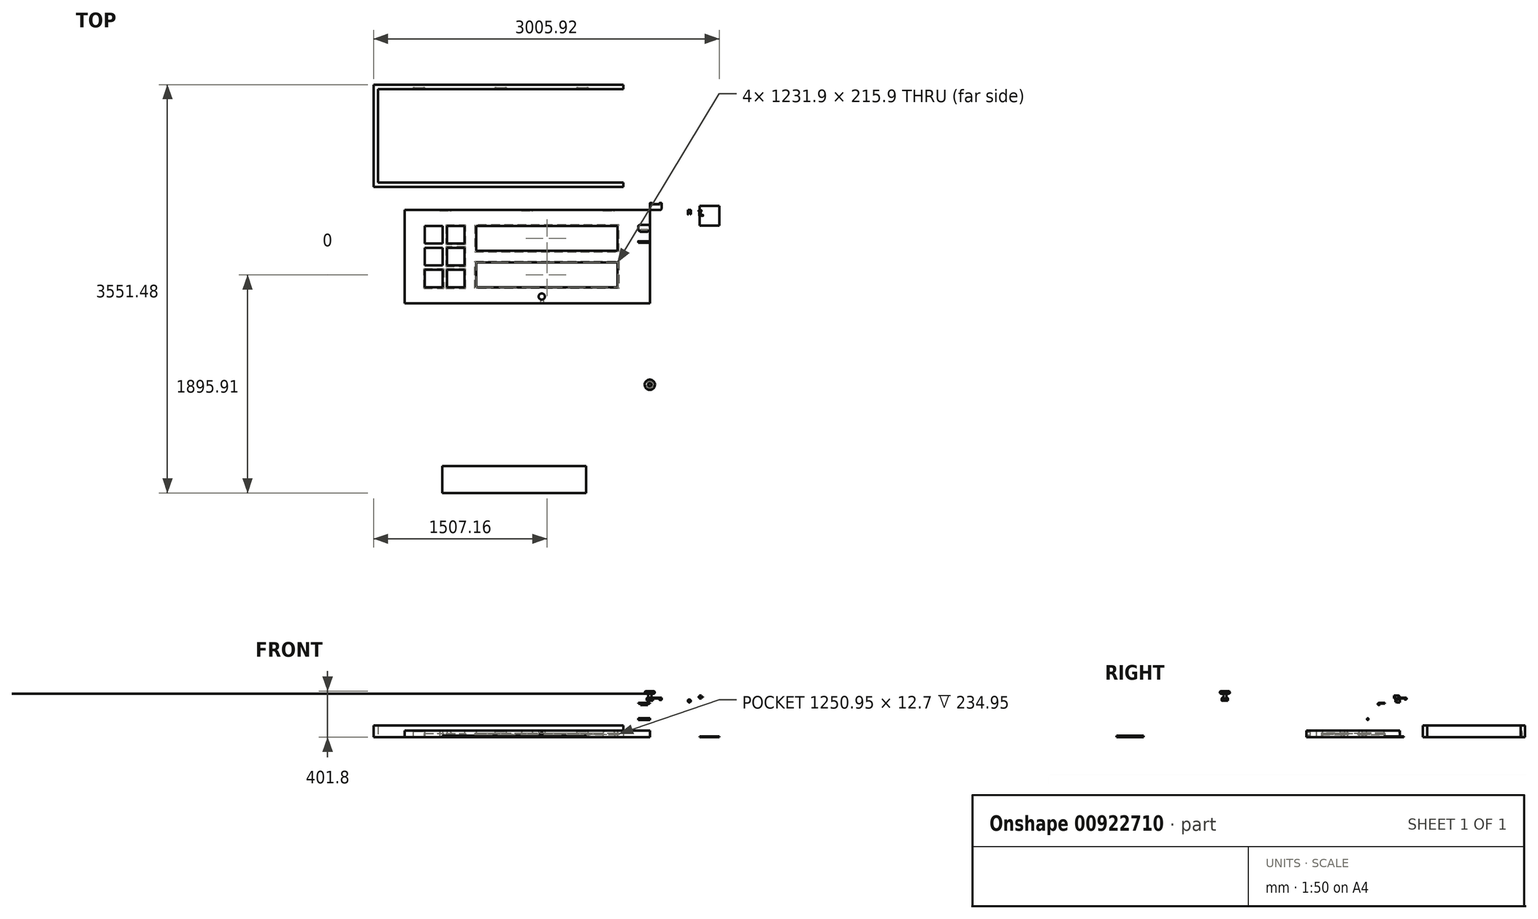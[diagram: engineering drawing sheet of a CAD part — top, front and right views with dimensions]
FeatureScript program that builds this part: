
annotation { "Feature Type Name" : "Feature", "Feature Type Description" : "" }
export const myFeature = defineFeature(function(context is Context, id is Id, definition is map)
    precondition{}
    {
        {
            var Q0;
            Q0=qCreatedBy(makeId("Top.planeOp"),FACE);
            var sketch = newSketch(context, id + "F0", { "sketchPlane" : qUnion([Q0])});
            skLineSegment(sketch, "E0", {"start": v(0, 0) * mm, "end": v(0, -812.8) * mm});
            skLineSegment(sketch, "E1", {"start": v(0, -812.8) * mm, "end": v(-2133.6, -812.8) * mm});
            skLineSegment(sketch, "E2", {"start": v(-2133.6, -812.8) * mm, "end": v(-2133.6, 0) * mm});
            skLineSegment(sketch, "E3", {"start": v(-2133.6, 0) * mm, "end": v(0, 0) * mm});
            skLineSegment(sketch, "E4.bottom", {"start": v(-1955.8, -673.1) * mm, "end": v(-1803.4, -673.1) * mm});
            skLineSegment(sketch, "E4.top", {"start": v(-1955.8, -139.7) * mm, "end": v(-1803.4, -139.7) * mm});
            skLineSegment(sketch, "E4.left", {"start": v(-1955.8, -673.1) * mm, "end": v(-1955.8, -520.7) * mm});
            skLineSegment(sketch, "E4.right", {"start": v(-1612.9, -673.1) * mm, "end": v(-1612.9, -520.7) * mm});
            skLineSegment(sketch, "E5", {"start": v(-1612.9, -482.6) * mm, "end": v(-1612.9, -330.2) * mm});
            skLineSegment(sketch, "E6.0.left", {"start": v(-1955.8, -482.6) * mm, "end": v(-1803.4, -482.6) * mm});
            skLineSegment(sketch, "E6.0.right", {"start": v(-1955.8, -520.7) * mm, "end": v(-1803.4, -520.7) * mm});
            skLineSegment(sketch, "E6.1.left", {"start": v(-1765.3, -139.7) * mm, "end": v(-1765.3, -292.1) * mm});
            skLineSegment(sketch, "E6.1.right", {"start": v(-1803.4, -139.7) * mm, "end": v(-1803.4, -292.1) * mm});
            skLineSegment(sketch, "E6.2.left", {"start": v(-1612.9, -330.2) * mm, "end": v(-1765.3, -330.2) * mm});
            skLineSegment(sketch, "E6.2.right", {"start": v(-1612.9, -292.1) * mm, "end": v(-1765.3, -292.1) * mm});
            skPoint(sketch, "E7.orphan", {"position": v(-1955.8, -351.36) * mm});
            skPoint(sketch, "E8.orphan", {"position": v(-1955.8, -461.44) * mm});
            skLineSegment(sketch, "E9.trimOffspring", {"start": v(-1803.4, -520.7) * mm, "end": v(-1803.4, -673.1) * mm});
            skLineSegment(sketch, "E10.trimOffspring", {"start": v(-1765.3, -520.7) * mm, "end": v(-1612.9, -520.7) * mm});
            skLineSegment(sketch, "E11.trimOffspring", {"start": v(-1765.3, -520.7) * mm, "end": v(-1765.3, -673.1) * mm});
            skLineSegment(sketch, "E12.trimOffspring", {"start": v(-1765.3, -482.6) * mm, "end": v(-1612.9, -482.6) * mm});
            skLineSegment(sketch, "E13.trimOffspring", {"start": v(-1803.4, -292.1) * mm, "end": v(-1955.8, -292.1) * mm});
            skLineSegment(sketch, "E14.trimOffspring", {"start": v(-1803.4, -330.2) * mm, "end": v(-1803.4, -482.6) * mm});
            skLineSegment(sketch, "E15.trimOffspring", {"start": v(-1803.4, -330.2) * mm, "end": v(-1955.8, -330.2) * mm});
            skLineSegment(sketch, "E16.trimOffspring", {"start": v(-1765.3, -330.2) * mm, "end": v(-1765.3, -482.6) * mm});
            skPoint(sketch, "E6.1.startCap.center.orphan", {"position": v(-1784.35, -139.7) * mm});
            skPoint(sketch, "E6.1.endCap.center.orphan", {"position": v(-1784.35, -673.1) * mm});
            skLineSegment(sketch, "E17.trimOffspring", {"start": v(-1955.8, -482.6) * mm, "end": v(-1955.8, -330.2) * mm});
            skLineSegment(sketch, "E18.trimOffspring", {"start": v(-1955.8, -292.1) * mm, "end": v(-1955.8, -139.7) * mm});
            skLineSegment(sketch, "E19.trimOffspring", {"start": v(-1612.9, -292.1) * mm, "end": v(-1612.9, -139.7) * mm});
            skLineSegment(sketch, "E20.trimOffspring", {"start": v(-1765.3, -673.1) * mm, "end": v(-1612.9, -673.1) * mm});
            skLineSegment(sketch, "E21.trimOffspring", {"start": v(-1765.3, -139.7) * mm, "end": v(-1612.9, -139.7) * mm});
            skLineSegment(sketch, "E22.bottom", {"start": v(-1511.3, -673.1) * mm, "end": v(-279.4, -673.1) * mm});
            skLineSegment(sketch, "E22.top", {"start": v(-1511.3, -139.7) * mm, "end": v(-279.4, -139.7) * mm});
            skLineSegment(sketch, "E22.left", {"start": v(-1511.3, -673.1) * mm, "end": v(-1511.3, -457.2) * mm});
            skLineSegment(sketch, "E22.right", {"start": v(-279.4, -673.1) * mm, "end": v(-279.4, -457.2) * mm});
            skLineSegment(sketch, "E23.0.left", {"start": v(-1511.3, -355.6) * mm, "end": v(-279.4, -355.6) * mm});
            skLineSegment(sketch, "E23.0.right", {"start": v(-1511.3, -457.2) * mm, "end": v(-279.4, -457.2) * mm});
            skPoint(sketch, "E24.start.orphan", {"position": v(-1511.3, -406.4) * mm});
            skLineSegment(sketch, "E25.trimOffspring", {"start": v(-1511.3, -355.6) * mm, "end": v(-1511.3, -139.7) * mm});
            skLineSegment(sketch, "E26.trimOffspring", {"start": v(-279.4, -355.6) * mm, "end": v(-279.4, -139.7) * mm});
            skPoint(sketch, "E23.0.endCap.center.orphan", {"position": v(-279.4, -406.4) * mm});
            skSolve(sketch);
        }
        {
            var Q0;
            Q0=makeQuery(id+"F0.imprint","IMPRINT",FACE,{"disambiguationData":[TD([[makeQuery(id+"F0.imprint","IMPRINT",EDGE,{"derivedFrom":sQuery(id+"F0.wireOp",EDGE,"E0")}),-1.0]])]});
            extrude(context, id + "F1", {"entities" : qUnion([Q0]), "depth" : 57.15 * mm, "offsetDistance" : 25.4 * mm});
        }
        {
            var Q0;
            Q0=qCreatedBy(makeId("Right.planeOp"),FACE);
            var sketch = newSketch(context, id + "F2", { "sketchPlane" : qUnion([Q0])});
            skLineSegment(sketch, "E27", {"start": v(41.82, 339.3) * mm, "end": v(0, 339.3) * mm});
            skLineSegment(sketch, "E28", {"start": v(0, 339.3) * mm, "end": v(0, 345.66) * mm});
            skLineSegment(sketch, "E29", {"start": v(0, 345.66) * mm, "end": v(50.8, 345.66) * mm});
            skArc(sketch, "E30", {"start": v(41.82, 339.3) * mm, "mid": v(56.3, 328.36) * mm, "end": v(50.8, 345.66) * mm});
            skCircle(sketch, "E31.0", {"center": v(50.8, 336.13) * mm, "radius": 6.99 * mm});
            skPoint(sketch, "E32.end.orphan", {"position": v(50.8, 339.3) * mm});
            skSolve(sketch);
        }
        {
            var Q0;
            Q0=makeQuery(id+"F2.imprint","IMPRINT",FACE,{"disambiguationData":[TD([[makeQuery(id+"F2.imprint","IMPRINT",EDGE,{"derivedFrom":sQuery(id+"F2.wireOp",EDGE,"E27")}),-1.0]])]});
            extrude(context, id + "F3", {"entities" : qUnion([Q0]), "depth" : 101.6 * mm, "offsetDistance" : 25.4 * mm});
        }
        {
            var Q0;
            Q0=makeQuery(id+"F3.opExtrude","CAP_FACE",FACE,{"disambiguationData":[OSD([sQuery(id+"F2.wireOp",EDGE,"E27"),sQuery(id+"F2.wireOp",EDGE,"E28"),sQuery(id+"F2.wireOp",EDGE,"E29"),sQuery(id+"F2.wireOp",EDGE,"E30"),sQuery(id+"F2.wireOp",EDGE,"E31.0")])],"isStart":false});
            cPlane(context, id + "F4", {"entities" : qUnion([Q0]), "cplaneType" : CPlaneType.OFFSET, "offset" : 19.05 * mm, "oppositeDirection" : true, "width" : 152.4 * mm, "height" : 152.4 * mm});
        }
        {
            var Q0;
            Q0=qCreatedBy(id+"F4.planeOp",FACE);
            var sketch = newSketch(context, id + "F5", { "sketchPlane" : qUnion([Q0])});
            skCircle(sketch, "E33", {"center": v(50.8, 336.13) * mm, "radius": 9.53 * mm});
            skLineSegment(sketch, "E34", {"start": v(50.8, 336.13) * mm, "end": v(50.8, 345.66) * mm});
            skSolve(sketch);
        }
        {
            var Q0;
            Q0 = qSketchRegion(id + "F5", true);
            extrude(context, id + "F6", {"entities" : qUnion([Q0]), "operationType" : NewBodyOperationType.REMOVE, "oppositeDirection" : true, "depth" : 63.5 * mm, "offsetDistance" : 25.4 * mm});
        }
        {
            var Q0;
            Q0=qCreatedBy(makeId("Right.planeOp"),FACE);
            var sketch = newSketch(context, id + "F7", { "sketchPlane" : qUnion([Q0])});
            skLineSegment(sketch, "E35", {"start": v(-172.18, 292.28) * mm, "end": v(-130.36, 292.28) * mm});
            skLineSegment(sketch, "E36", {"start": v(-130.36, 292.28) * mm, "end": v(-130.36, 298.63) * mm});
            skLineSegment(sketch, "E37", {"start": v(-130.36, 298.63) * mm, "end": v(-181.16, 298.63) * mm});
            skArc(sketch, "E38", {"start": v(-172.18, 292.28) * mm, "mid": v(-175.66, 296.88) * mm, "end": v(-181.16, 298.63) * mm});
            skPoint(sketch, "E39", {"position": v(-181.16, 298.63) * mm});
            skPoint(sketch, "E40.orphan", {"position": v(-181.16, 292.28) * mm});
            skSolve(sketch);
        }
        {
            var Q0;
            Q0 = qSketchRegion(id + "F7", true);
            extrude(context, id + "F8", {"entities" : qUnion([Q0]), "oppositeDirection" : true, "depth" : 101.6 * mm, "offsetDistance" : 25.4 * mm});
        }
        {
            var Q0;
            Q0=makeQuery(id+"F8.opExtrude","CAP_FACE",FACE,{"disambiguationData":[OSD([sQuery(id+"F7.wireOp",EDGE,"E35"),sQuery(id+"F7.wireOp",EDGE,"E36"),sQuery(id+"F7.wireOp",EDGE,"E37"),sQuery(id+"F7.wireOp",EDGE,"E38")])],"isStart":true});
            cPlane(context, id + "F9", {"entities" : qUnion([Q0]), "cplaneType" : CPlaneType.OFFSET, "offset" : 50.8 * mm, "oppositeDirection" : true, "width" : 152.4 * mm, "height" : 152.4 * mm});
        }
        {
            var Q0;
            Q0=qCreatedBy(id+"F9.planeOp",FACE);
            var sketch = newSketch(context, id + "F10", { "sketchPlane" : qUnion([Q0])});
            skCircle(sketch, "E41", {"center": v(-181.16, 289.1) * mm, "radius": 9.53 * mm});
            skPoint(sketch, "E42", {"position": v(-181.16, 298.63) * mm});
            skCircle(sketch, "E43.0", {"center": v(-181.16, 289.1) * mm, "radius": 6.99 * mm});
            skSolve(sketch);
        }
        {
            var Q0;
            Q0=makeQuery(id+"F10.imprint","IMPRINT",FACE,{"disambiguationData":[TD([[makeQuery(id+"F10.imprint","IMPRINT",EDGE,{"derivedFrom":sQuery(id+"F10.wireOp",EDGE,"E41")}),1.0]])]});
            extrude(context, id + "F11", {"entities" : qUnion([Q0]), "operationType" : NewBodyOperationType.ADD, "endBound" : BoundingType.SYMMETRIC, "depth" : 63.5 * mm, "offsetDistance" : 25.4 * mm});
        }
        {
            var Q0;
            Q0=qCreatedBy(makeId("Right.planeOp"),FACE);
            var sketch = newSketch(context, id + "F12", { "sketchPlane" : qUnion([Q0])});
            skCircle(sketch, "E44", {"center": v(-277.25, 157.74) * mm, "radius": 6.99 * mm});
            skSolve(sketch);
        }
        {
            var Q0;
            Q0 = qSketchRegion(id + "F12", true);
            extrude(context, id + "F13", {"entities" : qUnion([Q0]), "oppositeDirection" : true, "depth" : 101.6 * mm, "offsetDistance" : 25.4 * mm});
        }
        {
            var Q0;
            Q0=makeQuery(id+"F8.opExtrude","CAP_EDGE",EDGE,{"disambiguationData":[OSD([sQuery(id+"F7.wireOp",EDGE,"E36")])],"isStart":true});
            var Q1;
            Q1=makeQuery(id+"F8.opExtrude","CAP_EDGE",EDGE,{"disambiguationData":[OSD([sQuery(id+"F7.wireOp",EDGE,"E36")])],"isStart":false});
            var Q2;
            Q2=makeQuery(id+"F3.opExtrude","CAP_EDGE",EDGE,{"disambiguationData":[OSD([sQuery(id+"F2.wireOp",EDGE,"E28")])],"isStart":false});
            var Q3;
            Q3=makeQuery(id+"F3.opExtrude","CAP_EDGE",EDGE,{"disambiguationData":[OSD([sQuery(id+"F2.wireOp",EDGE,"E28")])],"isStart":true});
            fillet(context, id + "F14", {"entities" : qUnion([Q0, Q1, Q2, Q3]), "radius" : 12.7 * mm, "tangentPropagation" : true, "allowEdgeOverflow" : false});
        }
        {
            var Q0;
            Q0=makeQuery(id+"F1.opExtrude","SWEPT_FACE",FACE,{"disambiguationData":[OSD([sQuery(id+"F0.wireOp",EDGE,"E3")])]});
            var sketch = newSketch(context, id + "F15", { "sketchPlane" : qUnion([Q0])});
            skLineSegment(sketch, "E45", {"start": v(0, 0) * mm, "end": v(2133.6, 0) * mm});
            skLineSegment(sketch, "E46", {"start": v(2133.6, 0) * mm, "end": v(1422.4, 0) * mm});
            skLineSegment(sketch, "E47", {"start": v(1422.4, 0) * mm, "end": v(711.2, 0) * mm});
            skLineSegment(sketch, "E48.bottom", {"start": v(1016, 50.8) * mm, "end": v(1117.6, 50.8) * mm});
            skLineSegment(sketch, "E48.top", {"start": v(1016, 0) * mm, "end": v(1117.6, 0) * mm});
            skLineSegment(sketch, "E48.left", {"start": v(1016, 50.8) * mm, "end": v(1016, 0) * mm});
            skLineSegment(sketch, "E48.right", {"start": v(1117.6, 50.8) * mm, "end": v(1117.6, 0) * mm});
            skLineSegment(sketch, "E49.bottom", {"start": v(304.8, 50.8) * mm, "end": v(406.4, 50.8) * mm});
            skLineSegment(sketch, "E49.top", {"start": v(304.8, 0) * mm, "end": v(406.4, 0) * mm});
            skLineSegment(sketch, "E49.left", {"start": v(304.8, 50.8) * mm, "end": v(304.8, 0) * mm});
            skLineSegment(sketch, "E49.right", {"start": v(406.4, 50.8) * mm, "end": v(406.4, 0) * mm});
            skLineSegment(sketch, "E50.bottom", {"start": v(1727.2, 50.8) * mm, "end": v(1828.8, 50.8) * mm});
            skLineSegment(sketch, "E50.top", {"start": v(1727.2, 0) * mm, "end": v(1828.8, 0) * mm});
            skLineSegment(sketch, "E50.left", {"start": v(1727.2, 50.8) * mm, "end": v(1727.2, 0) * mm});
            skLineSegment(sketch, "E50.right", {"start": v(1828.8, 50.8) * mm, "end": v(1828.8, 0) * mm});
            skPoint(sketch, "E51", {"position": v(1066.8, 0) * mm});
            skPoint(sketch, "E52", {"position": v(355.6, 0) * mm});
            skPoint(sketch, "E53", {"position": v(1778, 0) * mm});
            skLineSegment(sketch, "E54", {"start": v(0, 0) * mm, "end": v(711.2, 0) * mm});
            skLineSegment(sketch, "E55", {"start": v(1422.4, 0) * mm, "end": v(2133.6, 0) * mm});
            skSolve(sketch);
        }
        {
            var Q0;
            Q0 = qSketchRegion(id + "F15", true);
            extrude(context, id + "F16", {"entities" : qUnion([Q0]), "operationType" : NewBodyOperationType.REMOVE, "oppositeDirection" : true, "depth" : 6.35 * mm, "offsetDistance" : 25.4 * mm});
        }
        {
            var Q0;
            Q0=makeQuery(id+"F16.boolean.opBoolean","COPY",EDGE,{"derivedFrom":makeQuery(id+"F16.opExtrude","SWEPT_EDGE",EDGE,{"disambiguationData":[OSD([sQuery(id+"F15.wireOp",EDGE,"E49.bottom"),sQuery(id+"F15.wireOp",EDGE,"E49.left")])]})});
            var Q1;
            Q1=makeQuery(id+"F16.boolean.opBoolean","COPY",EDGE,{"derivedFrom":makeQuery(id+"F16.opExtrude","SWEPT_EDGE",EDGE,{"disambiguationData":[OSD([sQuery(id+"F15.wireOp",EDGE,"E49.bottom"),sQuery(id+"F15.wireOp",EDGE,"E49.right")])]})});
            var Q2;
            Q2=makeQuery(id+"F16.boolean.opBoolean","COPY",EDGE,{"derivedFrom":makeQuery(id+"F16.opExtrude","SWEPT_EDGE",EDGE,{"disambiguationData":[OSD([sQuery(id+"F15.wireOp",EDGE,"E48.bottom"),sQuery(id+"F15.wireOp",EDGE,"E48.right")])]})});
            var Q3;
            Q3=makeQuery(id+"F16.boolean.opBoolean","COPY",EDGE,{"derivedFrom":makeQuery(id+"F16.opExtrude","SWEPT_EDGE",EDGE,{"disambiguationData":[OSD([sQuery(id+"F15.wireOp",EDGE,"E48.bottom"),sQuery(id+"F15.wireOp",EDGE,"E48.left")])]})});
            var Q4;
            Q4=makeQuery(id+"F16.boolean.opBoolean","COPY",EDGE,{"derivedFrom":makeQuery(id+"F16.opExtrude","SWEPT_EDGE",EDGE,{"disambiguationData":[OSD([sQuery(id+"F15.wireOp",EDGE,"E50.bottom"),sQuery(id+"F15.wireOp",EDGE,"E50.left")])]})});
            var Q5;
            Q5=makeQuery(id+"F16.boolean.opBoolean","COPY",EDGE,{"derivedFrom":makeQuery(id+"F16.opExtrude","SWEPT_EDGE",EDGE,{"disambiguationData":[OSD([sQuery(id+"F15.wireOp",EDGE,"E50.bottom"),sQuery(id+"F15.wireOp",EDGE,"E50.right")])]})});
            fillet(context, id + "F17", {"entities" : qUnion([Q0, Q1, Q2, Q3, Q4, Q5]), "radius" : 12.7 * mm, "tangentPropagation" : true, "allowEdgeOverflow" : false});
        }
        {
            var Q0;
            Q0=qCreatedBy(makeId("Top.planeOp"),FACE);
            var sketch = newSketch(context, id + "F18", { "sketchPlane" : qUnion([Q0])});
            skLineSegment(sketch, "E56.bottom", {"start": v(-2364.4, 239.52) * mm, "end": v(-230.8, 239.52) * mm});
            skLineSegment(sketch, "E56.top", {"start": v(-2364.4, 1052.32) * mm, "end": v(-230.8, 1052.32) * mm});
            skLineSegment(sketch, "E56.left", {"start": v(-2364.4, 239.52) * mm, "end": v(-2364.4, 1052.32) * mm});
            skLineSegment(sketch, "E57.0", {"start": v(-2402.5, 201.42) * mm, "end": v(-2402.5, 1090.42) * mm});
            skLineSegment(sketch, "E57.1", {"start": v(-2402.5, 201.42) * mm, "end": v(-230.8, 201.42) * mm});
            skLineSegment(sketch, "E57.3", {"start": v(-2402.5, 1090.42) * mm, "end": v(-230.8, 1090.42) * mm});
            skLineSegment(sketch, "E58", {"start": v(-230.8, 239.52) * mm, "end": v(-230.8, 201.42) * mm});
            skLineSegment(sketch, "E59", {"start": v(-230.8, 201.42) * mm, "end": v(-230.8, 239.52) * mm});
            skLineSegment(sketch, "E60.trimOffspring", {"start": v(-230.8, 1052.32) * mm, "end": v(-230.8, 1090.42) * mm});
            skSolve(sketch);
        }
        {
            var Q0;
            Q0 = qSketchRegion(id + "F18", true);
            extrude(context, id + "F19", {"entities" : qUnion([Q0]), "depth" : 101.6 * mm, "offsetDistance" : 25.4 * mm});
        }
        {
            var Q0;
            Q0=makeQuery(id+"F19.opExtrude","SWEPT_FACE",FACE,{"disambiguationData":[OSD([sQuery(id+"F18.wireOp",EDGE,"E56.top")])]});
            var sketch = newSketch(context, id + "F20", { "sketchPlane" : qUnion([Q0])});
            skLineSegment(sketch, "E61", {"start": v(-2364.4, 0) * mm, "end": v(-230.8, 0) * mm});
            skLineSegment(sketch, "E62", {"start": v(-230.8, 0) * mm, "end": v(-942, 0) * mm});
            skLineSegment(sketch, "E63", {"start": v(-942, 0) * mm, "end": v(-1653.2, 0) * mm});
            skLineSegment(sketch, "E64.bottom", {"start": v(-1348.4, 50.8) * mm, "end": v(-1246.8, 50.8) * mm});
            skLineSegment(sketch, "E64.top", {"start": v(-1348.4, 0) * mm, "end": v(-1246.8, 0) * mm});
            skLineSegment(sketch, "E64.left", {"start": v(-1348.4, 50.8) * mm, "end": v(-1348.4, 0) * mm});
            skLineSegment(sketch, "E64.right", {"start": v(-1246.8, 50.8) * mm, "end": v(-1246.8, 0) * mm});
            skLineSegment(sketch, "E65.bottom", {"start": v(-2059.6, 50.8) * mm, "end": v(-1958, 50.8) * mm});
            skLineSegment(sketch, "E65.top", {"start": v(-2059.6, 0) * mm, "end": v(-1958, 0) * mm});
            skLineSegment(sketch, "E65.left", {"start": v(-2059.6, 50.8) * mm, "end": v(-2059.6, 0) * mm});
            skLineSegment(sketch, "E65.right", {"start": v(-1958, 50.8) * mm, "end": v(-1958, 0) * mm});
            skLineSegment(sketch, "E66.bottom", {"start": v(-637.2, 50.8) * mm, "end": v(-535.6, 50.8) * mm});
            skLineSegment(sketch, "E66.top", {"start": v(-637.2, 0) * mm, "end": v(-535.6, 0) * mm});
            skLineSegment(sketch, "E66.left", {"start": v(-637.2, 50.8) * mm, "end": v(-637.2, 0) * mm});
            skLineSegment(sketch, "E66.right", {"start": v(-535.6, 50.8) * mm, "end": v(-535.6, 0) * mm});
            skPoint(sketch, "E67", {"position": v(-1297.6, 0) * mm});
            skPoint(sketch, "E68", {"position": v(-2008.8, 0) * mm});
            skPoint(sketch, "E69", {"position": v(-586.4, 0) * mm});
            skLineSegment(sketch, "E70", {"start": v(-2364.4, 0) * mm, "end": v(-1653.2, 0) * mm});
            skLineSegment(sketch, "E71", {"start": v(-942, 0) * mm, "end": v(-230.8, 0) * mm});
            skSolve(sketch);
        }
        {
            var Q0;
            Q0 = qSketchRegion(id + "F20", true);
            extrude(context, id + "F21", {"entities" : qUnion([Q0]), "operationType" : NewBodyOperationType.REMOVE, "oppositeDirection" : true, "depth" : 12.7 * mm, "offsetDistance" : 25.4 * mm});
        }
        {
            var Q0;
            Q0=makeQuery(id+"F21.boolean.opBoolean","COPY",EDGE,{"derivedFrom":makeQuery(id+"F21.opExtrude","SWEPT_EDGE",EDGE,{"disambiguationData":[OSD([sQuery(id+"F20.wireOp",EDGE,"E64.bottom"),sQuery(id+"F20.wireOp",EDGE,"E64.left")])]})});
            var Q1;
            Q1=makeQuery(id+"F21.boolean.opBoolean","COPY",EDGE,{"derivedFrom":makeQuery(id+"F21.opExtrude","SWEPT_EDGE",EDGE,{"disambiguationData":[OSD([sQuery(id+"F20.wireOp",EDGE,"E64.bottom"),sQuery(id+"F20.wireOp",EDGE,"E64.right")])]})});
            var Q2;
            Q2=makeQuery(id+"F21.boolean.opBoolean","COPY",EDGE,{"derivedFrom":makeQuery(id+"F21.opExtrude","SWEPT_EDGE",EDGE,{"disambiguationData":[OSD([sQuery(id+"F20.wireOp",EDGE,"E65.bottom"),sQuery(id+"F20.wireOp",EDGE,"E65.right")])]})});
            var Q3;
            Q3=makeQuery(id+"F21.boolean.opBoolean","COPY",EDGE,{"derivedFrom":makeQuery(id+"F21.opExtrude","SWEPT_EDGE",EDGE,{"disambiguationData":[OSD([sQuery(id+"F20.wireOp",EDGE,"E65.bottom"),sQuery(id+"F20.wireOp",EDGE,"E65.left")])]})});
            var Q4;
            Q4=makeQuery(id+"F21.boolean.opBoolean","COPY",EDGE,{"derivedFrom":makeQuery(id+"F21.opExtrude","SWEPT_EDGE",EDGE,{"disambiguationData":[OSD([sQuery(id+"F20.wireOp",EDGE,"E66.bottom"),sQuery(id+"F20.wireOp",EDGE,"E66.left")])]})});
            var Q5;
            Q5=makeQuery(id+"F21.boolean.opBoolean","COPY",EDGE,{"derivedFrom":makeQuery(id+"F21.opExtrude","SWEPT_EDGE",EDGE,{"disambiguationData":[OSD([sQuery(id+"F20.wireOp",EDGE,"E66.bottom"),sQuery(id+"F20.wireOp",EDGE,"E66.right")])]})});
            fillet(context, id + "F22", {"entities" : qUnion([Q0, Q1, Q2, Q3, Q4, Q5]), "radius" : 12.7 * mm, "tangentPropagation" : true, "allowEdgeOverflow" : false});
        }
        {
            var Q0;
            Q0=makeQuery(id+"F1.opExtrude","CAP_FACE",FACE,{"disambiguationData":[OSD([sQuery(id+"F0.wireOp",EDGE,"E0"),sQuery(id+"F0.wireOp",EDGE,"E1"),sQuery(id+"F0.wireOp",EDGE,"E2"),sQuery(id+"F0.wireOp",EDGE,"E3"),sQuery(id+"F0.wireOp",EDGE,"E4.bottom"),sQuery(id+"F0.wireOp",EDGE,"E4.top"),sQuery(id+"F0.wireOp",EDGE,"E4.left"),sQuery(id+"F0.wireOp",EDGE,"E4.right"),sQuery(id+"F0.wireOp",EDGE,"E6.0.left"),sQuery(id+"F0.wireOp",EDGE,"E6.0.right"),sQuery(id+"F0.wireOp",EDGE,"E6.1.left"),sQuery(id+"F0.wireOp",EDGE,"E6.1.right"),sQuery(id+"F0.wireOp",EDGE,"E6.2.left"),sQuery(id+"F0.wireOp",EDGE,"E6.2.right"),sQuery(id+"F0.wireOp",EDGE,"E9.trimOffspring"),sQuery(id+"F0.wireOp",EDGE,"E10.trimOffspring"),sQuery(id+"F0.wireOp",EDGE,"E11.trimOffspring"),sQuery(id+"F0.wireOp",EDGE,"E12.trimOffspring"),sQuery(id+"F0.wireOp",EDGE,"E13.trimOffspring"),sQuery(id+"F0.wireOp",EDGE,"E14.trimOffspring"),sQuery(id+"F0.wireOp",EDGE,"E15.trimOffspring"),sQuery(id+"F0.wireOp",EDGE,"E16.trimOffspring"),sQuery(id+"F0.wireOp",EDGE,"E17.trimOffspring"),sQuery(id+"F0.wireOp",EDGE,"E18.trimOffspring"),sQuery(id+"F0.wireOp",EDGE,"E19.trimOffspring"),sQuery(id+"F0.wireOp",EDGE,"E5"),sQuery(id+"F0.wireOp",EDGE,"E20.trimOffspring"),sQuery(id+"F0.wireOp",EDGE,"E21.trimOffspring"),sQuery(id+"F0.wireOp",EDGE,"E22.bottom"),sQuery(id+"F0.wireOp",EDGE,"E22.top"),sQuery(id+"F0.wireOp",EDGE,"E22.left"),sQuery(id+"F0.wireOp",EDGE,"E22.right"),sQuery(id+"F0.wireOp",EDGE,"E23.0.left"),sQuery(id+"F0.wireOp",EDGE,"E23.0.right"),sQuery(id+"F0.wireOp",EDGE,"E25.trimOffspring"),sQuery(id+"F0.wireOp",EDGE,"E26.trimOffspring")])],"isStart":true});
            var sketch = newSketch(context, id + "F23", { "sketchPlane" : qUnion([Q0])});
            skCircle(sketch, "E72", {"center": v(-939.8, 752.48) * mm, "radius": 26.99 * mm});
            skSolve(sketch);
        }
        {
            var Q0;
            Q0 = qSketchRegion(id + "F23", true);
            extrude(context, id + "F24", {"entities" : qUnion([Q0]), "operationType" : NewBodyOperationType.REMOVE, "oppositeDirection" : true, "depth" : 393.7 * mm, "offsetDistance" : 25.4 * mm});
        }
        {
            var Q0;
            Q0=makeQuery(id+"F1.opExtrude","SWEPT_FACE",FACE,{"disambiguationData":[OSD([sQuery(id+"F0.wireOp",EDGE,"E1")])]});
            var sketch = newSketch(context, id + "F25", { "sketchPlane" : qUnion([Q0])});
            skLineSegment(sketch, "E73", {"start": v(0, 28.58) * mm, "end": v(-2133.6, 28.58) * mm});
            skCircle(sketch, "E74", {"center": v(-939.8, 28.58) * mm, "radius": 12.7 * mm});
            skSolve(sketch);
        }
        {
            var Q0;
            Q0 = qSketchRegion(id + "F25", true);
            extrude(context, id + "F26", {"entities" : qUnion([Q0]), "operationType" : NewBodyOperationType.REMOVE, "oppositeDirection" : true, "depth" : 57.66 * mm, "offsetDistance" : 25.4 * mm});
        }
        {
            var Q0;
            Q0=qCreatedBy(makeId("Right.planeOp"),FACE);
            var sketch = newSketch(context, id + "F27", { "sketchPlane" : qUnion([Q0])});
            skLineSegment(sketch, "E75", {"start": v(-1520.1, 400.98) * mm, "end": v(-1520.1, 337.48) * mm});
            skLineSegment(sketch, "E76", {"start": v(-1520.1, 337.48) * mm, "end": v(-1548.67, 337.48) * mm});
            skFitSpline(sketch, "E77", {"points": [v(-1520.1, 400.98) * mm, v(-1554.77, 400.98) * mm, v(-1560.6, 397.47) * mm, v(-1564.63, 389.36) * mm, v(-1559.88, 382.56) * mm, v(-1549.73, 378.95) * mm, v(-1537.55, 378.37) * mm, v(-1533.98, 372.76) * mm, v(-1533.75, 362.9) * mm, v(-1533.53, 355.07) * mm, v(-1534.36, 348.8) * mm, v(-1538.28, 345.15) * mm, v(-1542.88, 342.93) * mm, v(-1545.86, 340.6) * mm, v(-1548.67, 337.48) * mm], "startDerivative": vector(-293.12, 14.72) * mm, "endDerivative": vector(-55.38, -64.96) * mm});
            skSolve(sketch);
        }
        {
            var Q0;
            Q0 = qSketchRegion(id + "F27", true);
            var Q1;
            Q1=sQuery(id+"F27.wireOp",EDGE,"E75");
            revolve(context, id + "F28", {"surfaceOperationType" : NewSurfaceOperationType.NEW, "entities" : qUnion([Q0]), "axis" : qUnion([Q1]), "revolveType" : RevolveType.FULL});
        }
        {
            var Q0;
            Q0=qCreatedBy(makeId("Top.planeOp"),FACE);
            var sketch = newSketch(context, id + "F29", { "sketchPlane" : qUnion([Q0])});
            skLineSegment(sketch, "E78.bottom", {"start": v(-1796.5, -2235.63) * mm, "end": v(-564.6, -2235.63) * mm});
            skLineSegment(sketch, "E78.top", {"start": v(-1796.5, -2451.53) * mm, "end": v(-564.6, -2451.53) * mm});
            skLineSegment(sketch, "E78.left", {"start": v(-1796.5, -2235.63) * mm, "end": v(-1796.5, -2451.53) * mm});
            skLineSegment(sketch, "E78.right", {"start": v(-564.6, -2235.63) * mm, "end": v(-564.6, -2451.53) * mm});
            skLineSegment(sketch, "E79.0", {"start": v(-1806.03, -2226.1) * mm, "end": v(-1806.03, -2461.06) * mm});
            skLineSegment(sketch, "E79.1", {"start": v(-1806.03, -2226.1) * mm, "end": v(-555.08, -2226.1) * mm});
            skLineSegment(sketch, "E79.2", {"start": v(-555.08, -2226.1) * mm, "end": v(-555.08, -2461.06) * mm});
            skLineSegment(sketch, "E79.3", {"start": v(-1806.03, -2461.06) * mm, "end": v(-555.08, -2461.06) * mm});
            skSolve(sketch);
        }
        {
            var Q0;
            Q0=makeQuery(id+"F1.opExtrude","SWEPT_FACE",FACE,{"disambiguationData":[OSD([sQuery(id+"F0.wireOp",EDGE,"E0")])]});
            cPlane(context, id + "F30", {"entities" : qUnion([Q0]), "cplaneType" : CPlaneType.OFFSET, "offset" : 627.38 * mm, "oppositeDirection" : true, "width" : 152.4 * mm, "height" : 152.4 * mm});
        }
        {
            var Q0;
            Q0=qCreatedBy(id+"F30.planeOp",FACE);
            var sketch = newSketch(context, id + "F31", { "sketchPlane" : qUnion([Q0])});
            skLineSegment(sketch, "E80", {"start": v(-457.2, 0) * mm, "end": v(-457.2, 57.15) * mm});
            skLineSegment(sketch, "E81", {"start": v(-355.6, 57.15) * mm, "end": v(-355.6, 0) * mm});
            skLineSegment(sketch, "E82.bottom", {"start": v(-447.68, 34.93) * mm, "end": v(-457.2, 34.93) * mm});
            skLineSegment(sketch, "E82.top", {"start": v(-447.68, 22.23) * mm, "end": v(-457.2, 22.23) * mm});
            skLineSegment(sketch, "E82.left", {"start": v(-447.68, 34.93) * mm, "end": v(-447.68, 22.23) * mm});
            skLineSegment(sketch, "E82.right", {"start": v(-457.2, 34.93) * mm, "end": v(-457.2, 22.23) * mm});
            skPoint(sketch, "E83", {"position": v(-457.2, 28.58) * mm});
            skLineSegment(sketch, "E84", {"start": v(-457.2, 22.23) * mm, "end": v(-459.65, 22.23) * mm});
            skLineSegment(sketch, "E85", {"start": v(-459.65, 22.23) * mm, "end": v(-459.65, 34.93) * mm});
            skLineSegment(sketch, "E86", {"start": v(-459.65, 34.93) * mm, "end": v(-457.2, 34.93) * mm});
            skSolve(sketch);
        }
        {
            var Q0;
            Q0=makeQuery(id+"F29.imprint","IMPRINT",FACE,{"disambiguationData":[TD([[makeQuery(id+"F29.imprint","IMPRINT",EDGE,{"derivedFrom":sQuery(id+"F29.wireOp",EDGE,"E78.bottom")}),-1.0]])]});
            var Q1;
            Q1=makeQuery(id+"F29.imprint","IMPRINT",FACE,{"disambiguationData":[TD([[makeQuery(id+"F29.imprint","IMPRINT",EDGE,{"derivedFrom":sQuery(id+"F29.wireOp",EDGE,"E78.bottom")}),1.0]])]});
            extrude(context, id + "F32", {"entities" : qUnion([Q0, Q1]), "depth" : 12.7 * mm, "offsetDistance" : 25.4 * mm});
        }
        {
            var Q0;
            Q0 = qSketchRegion(id + "F31", true);
            var Q1;
            Q1=makeQuery(id+"F1.opExtrude","CAP_EDGE",EDGE,{"disambiguationData":[OSD([sQuery(id+"F0.wireOp",EDGE,"E23.0.right")])],"isStart":true});
            var Q2;
            Q2=makeQuery(id+"F1.opExtrude","CAP_EDGE",EDGE,{"disambiguationData":[OSD([sQuery(id+"F0.wireOp",EDGE,"E22.left")])],"isStart":true});
            var Q3;
            Q3=makeQuery(id+"F1.opExtrude","CAP_EDGE",EDGE,{"disambiguationData":[OSD([sQuery(id+"F0.wireOp",EDGE,"E22.bottom")])],"isStart":true});
            var Q4;
            Q4=makeQuery(id+"F1.opExtrude","CAP_EDGE",EDGE,{"disambiguationData":[OSD([sQuery(id+"F0.wireOp",EDGE,"E22.right")])],"isStart":true});
            sweep(context, id + "F33", {"operationType" : NewBodyOperationType.REMOVE, "profiles" : qUnion([Q0]), "path" : qUnion([Q1, Q2, Q3, Q4])});
        }
        {
            var Q0;
            Q0=qCreatedBy(id+"F30.planeOp",FACE);
            var sketch = newSketch(context, id + "F34", { "sketchPlane" : qUnion([Q0])});
            skLineSegment(sketch, "E87", {"start": v(-355.6, 57.15) * mm, "end": v(-355.6, 0) * mm});
            skLineSegment(sketch, "E88.bottom", {"start": v(-355.6, 34.93) * mm, "end": v(-365.13, 34.93) * mm});
            skLineSegment(sketch, "E88.top", {"start": v(-355.6, 22.23) * mm, "end": v(-365.13, 22.23) * mm});
            skLineSegment(sketch, "E88.left", {"start": v(-355.6, 34.92) * mm, "end": v(-355.6, 22.23) * mm});
            skLineSegment(sketch, "E88.right", {"start": v(-365.13, 34.92) * mm, "end": v(-365.13, 22.23) * mm});
            skPoint(sketch, "E89", {"position": v(-355.6, 28.58) * mm});
            skSolve(sketch);
        }
        {
            var Q0;
            Q0 = qSketchRegion(id + "F34", true);
            var Q1;
            Q1=makeQuery(id+"F1.opExtrude","CAP_EDGE",EDGE,{"disambiguationData":[OSD([sQuery(id+"F0.wireOp",EDGE,"E23.0.left")])],"isStart":true});
            var Q2;
            Q2=makeQuery(id+"F1.opExtrude","CAP_EDGE",EDGE,{"disambiguationData":[OSD([sQuery(id+"F0.wireOp",EDGE,"E25.trimOffspring")])],"isStart":true});
            var Q3;
            Q3=makeQuery(id+"F1.opExtrude","CAP_EDGE",EDGE,{"disambiguationData":[OSD([sQuery(id+"F0.wireOp",EDGE,"E22.top")])],"isStart":true});
            var Q4;
            Q4=makeQuery(id+"F1.opExtrude","CAP_EDGE",EDGE,{"disambiguationData":[OSD([sQuery(id+"F0.wireOp",EDGE,"E26.trimOffspring")])],"isStart":true});
            sweep(context, id + "F35", {"operationType" : NewBodyOperationType.REMOVE, "profiles" : qUnion([Q0]), "path" : qUnion([Q1, Q2, Q3, Q4])});
        }
        {
            var Q0;
            Q0=makeQuery(id+"F1.opExtrude","CAP_FACE",FACE,{"disambiguationData":[OSD([sQuery(id+"F0.wireOp",EDGE,"E0"),sQuery(id+"F0.wireOp",EDGE,"E1"),sQuery(id+"F0.wireOp",EDGE,"E2"),sQuery(id+"F0.wireOp",EDGE,"E3"),sQuery(id+"F0.wireOp",EDGE,"E4.bottom"),sQuery(id+"F0.wireOp",EDGE,"E4.top"),sQuery(id+"F0.wireOp",EDGE,"E4.left"),sQuery(id+"F0.wireOp",EDGE,"E4.right"),sQuery(id+"F0.wireOp",EDGE,"E6.0.left"),sQuery(id+"F0.wireOp",EDGE,"E6.0.right"),sQuery(id+"F0.wireOp",EDGE,"E6.1.left"),sQuery(id+"F0.wireOp",EDGE,"E6.1.right"),sQuery(id+"F0.wireOp",EDGE,"E6.2.left"),sQuery(id+"F0.wireOp",EDGE,"E6.2.right"),sQuery(id+"F0.wireOp",EDGE,"E9.trimOffspring"),sQuery(id+"F0.wireOp",EDGE,"E10.trimOffspring"),sQuery(id+"F0.wireOp",EDGE,"E11.trimOffspring"),sQuery(id+"F0.wireOp",EDGE,"E12.trimOffspring"),sQuery(id+"F0.wireOp",EDGE,"E13.trimOffspring"),sQuery(id+"F0.wireOp",EDGE,"E14.trimOffspring"),sQuery(id+"F0.wireOp",EDGE,"E15.trimOffspring"),sQuery(id+"F0.wireOp",EDGE,"E16.trimOffspring"),sQuery(id+"F0.wireOp",EDGE,"E17.trimOffspring"),sQuery(id+"F0.wireOp",EDGE,"E18.trimOffspring"),sQuery(id+"F0.wireOp",EDGE,"E19.trimOffspring"),sQuery(id+"F0.wireOp",EDGE,"E5"),sQuery(id+"F0.wireOp",EDGE,"E20.trimOffspring"),sQuery(id+"F0.wireOp",EDGE,"E21.trimOffspring"),sQuery(id+"F0.wireOp",EDGE,"E22.bottom"),sQuery(id+"F0.wireOp",EDGE,"E22.top"),sQuery(id+"F0.wireOp",EDGE,"E22.left"),sQuery(id+"F0.wireOp",EDGE,"E22.right"),sQuery(id+"F0.wireOp",EDGE,"E23.0.left"),sQuery(id+"F0.wireOp",EDGE,"E23.0.right"),sQuery(id+"F0.wireOp",EDGE,"E25.trimOffspring"),sQuery(id+"F0.wireOp",EDGE,"E26.trimOffspring")])],"isStart":true});
            var sketch = newSketch(context, id + "F36", { "sketchPlane" : qUnion([Q0])});
            skLineSegment(sketch, "E90.0.0", {"start": v(-1828.8, 6.35) * mm, "end": v(-1727.2, 6.35) * mm});
            skLineSegment(sketch, "E90.0.1", {"start": v(-1727.2, 6.35) * mm, "end": v(-1727.2, 0) * mm});
            skLineSegment(sketch, "E90.0.2", {"start": v(-1727.2, 0) * mm, "end": v(-1117.6, 0) * mm});
            skLineSegment(sketch, "E90.0.3", {"start": v(-1117.6, 0) * mm, "end": v(-1117.6, 6.35) * mm});
            skLineSegment(sketch, "E90.0.4", {"start": v(-1117.6, 6.35) * mm, "end": v(-1016, 6.35) * mm});
            skLineSegment(sketch, "E90.0.5", {"start": v(-1016, 6.35) * mm, "end": v(-1016, 0) * mm});
            skLineSegment(sketch, "E90.0.6", {"start": v(-1016, 0) * mm, "end": v(-406.4, 0) * mm});
            skLineSegment(sketch, "E90.0.7", {"start": v(-406.4, 0) * mm, "end": v(-406.4, 6.35) * mm});
            skLineSegment(sketch, "E90.0.8", {"start": v(-406.4, 6.35) * mm, "end": v(-304.8, 6.35) * mm});
            skLineSegment(sketch, "E90.0.9", {"start": v(-304.8, 6.35) * mm, "end": v(-304.8, 0) * mm});
            skLineSegment(sketch, "E90.0.10", {"start": v(-304.8, 0) * mm, "end": v(0, 0) * mm});
            skLineSegment(sketch, "E90.0.11", {"start": v(0, 0) * mm, "end": v(0, 812.8) * mm});
            skLineSegment(sketch, "E90.0.12", {"start": v(0, 812.8) * mm, "end": v(-2133.6, 812.8) * mm});
            skLineSegment(sketch, "E90.0.13", {"start": v(-2133.6, 812.8) * mm, "end": v(-2133.6, 0) * mm});
            skLineSegment(sketch, "E90.0.14", {"start": v(-2133.6, 0) * mm, "end": v(-1828.8, 0) * mm});
            skLineSegment(sketch, "E90.0.15", {"start": v(-1828.8, 0) * mm, "end": v(-1828.8, 6.35) * mm});
            skLineSegment(sketch, "E91.0", {"start": v(-1955.8, 673.1) * mm, "end": v(-1955.8, 520.7) * mm});
            skLineSegment(sketch, "E92.0", {"start": v(-1955.8, 673.1) * mm, "end": v(-1803.4, 673.1) * mm});
            skLineSegment(sketch, "E93.0", {"start": v(-1803.4, 520.7) * mm, "end": v(-1803.4, 673.1) * mm});
            skLineSegment(sketch, "E94.0", {"start": v(-1955.8, 520.7) * mm, "end": v(-1803.4, 520.7) * mm});
            skLineSegment(sketch, "E95.0.0", {"start": v(-1803.4, 482.6) * mm, "end": v(-1955.8, 482.6) * mm});
            skLineSegment(sketch, "E95.0.2", {"start": v(-1955.8, 482.6) * mm, "end": v(-1803.4, 482.6) * mm});
            skLineSegment(sketch, "E96.0", {"start": v(-1955.8, 482.6) * mm, "end": v(-1955.8, 330.2) * mm});
            skLineSegment(sketch, "E97.0", {"start": v(-1803.4, 330.2) * mm, "end": v(-1955.8, 330.2) * mm});
            skLineSegment(sketch, "E98.0.0", {"start": v(-1803.4, 292.1) * mm, "end": v(-1955.8, 292.1) * mm});
            skLineSegment(sketch, "E98.0.2", {"start": v(-1955.8, 292.1) * mm, "end": v(-1803.4, 292.1) * mm});
            skLineSegment(sketch, "E99.0", {"start": v(-1955.8, 292.1) * mm, "end": v(-1955.8, 139.7) * mm});
            skLineSegment(sketch, "E100.0", {"start": v(-1955.8, 139.7) * mm, "end": v(-1803.4, 139.7) * mm});
            skLineSegment(sketch, "E101.0", {"start": v(-1803.4, 139.7) * mm, "end": v(-1803.4, 292.1) * mm});
            skLineSegment(sketch, "E102.0", {"start": v(-1803.4, 330.2) * mm, "end": v(-1803.4, 482.6) * mm});
            skLineSegment(sketch, "E103.0", {"start": v(-1765.3, 330.2) * mm, "end": v(-1765.3, 482.6) * mm});
            skLineSegment(sketch, "E104.0", {"start": v(-1765.3, 139.7) * mm, "end": v(-1765.3, 292.1) * mm});
            skLineSegment(sketch, "E105.0", {"start": v(-1612.9, 292.1) * mm, "end": v(-1765.3, 292.1) * mm});
            skLineSegment(sketch, "E106.0", {"start": v(-1612.9, 330.2) * mm, "end": v(-1765.3, 330.2) * mm});
            skPoint(sketch, "E107.0", {"position": v(-1689.1, 139.7) * mm});
            skPoint(sketch, "E108.0", {"position": v(-1612.9, 215.9) * mm});
            skPoint(sketch, "E109.0", {"position": v(-1612.9, 406.4) * mm});
            skPoint(sketch, "E110.0", {"position": v(-1689.1, 482.6) * mm});
            skLineSegment(sketch, "E111.0", {"start": v(-1765.3, 520.7) * mm, "end": v(-1612.9, 520.7) * mm});
            skLineSegment(sketch, "E112.0", {"start": v(-1765.3, 520.7) * mm, "end": v(-1765.3, 673.1) * mm});
            skLineSegment(sketch, "E113.0", {"start": v(-1765.3, 673.1) * mm, "end": v(-1612.9, 673.1) * mm});
            skPoint(sketch, "E114.0", {"position": v(-1612.9, 596.9) * mm});
            skLineSegment(sketch, "E115.0", {"start": v(-1612.9, 673.1) * mm, "end": v(-1612.9, 520.7) * mm});
            skLineSegment(sketch, "E116.0", {"start": v(-1965.33, 301.63) * mm, "end": v(-1965.33, 130.18) * mm});
            skLineSegment(sketch, "E116.1", {"start": v(-1965.33, 301.63) * mm, "end": v(-1793.88, 301.63) * mm});
            skLineSegment(sketch, "E116.2", {"start": v(-1793.88, 130.18) * mm, "end": v(-1793.88, 301.63) * mm});
            skLineSegment(sketch, "E116.3", {"start": v(-1965.33, 130.18) * mm, "end": v(-1793.88, 130.18) * mm});
            skLineSegment(sketch, "E117.0", {"start": v(-1965.33, 492.13) * mm, "end": v(-1965.33, 320.68) * mm});
            skLineSegment(sketch, "E117.1", {"start": v(-1793.88, 492.13) * mm, "end": v(-1965.33, 492.13) * mm});
            skLineSegment(sketch, "E117.2", {"start": v(-1793.88, 320.68) * mm, "end": v(-1793.88, 492.13) * mm});
            skLineSegment(sketch, "E117.3", {"start": v(-1793.88, 320.68) * mm, "end": v(-1965.33, 320.68) * mm});
            skLineSegment(sketch, "E118.0", {"start": v(-1965.33, 682.63) * mm, "end": v(-1965.33, 511.18) * mm});
            skLineSegment(sketch, "E118.1", {"start": v(-1965.33, 682.63) * mm, "end": v(-1793.87, 682.63) * mm});
            skLineSegment(sketch, "E118.2", {"start": v(-1793.88, 511.18) * mm, "end": v(-1793.87, 682.63) * mm});
            skLineSegment(sketch, "E118.3", {"start": v(-1965.33, 511.18) * mm, "end": v(-1793.88, 511.18) * mm});
            skLineSegment(sketch, "E119.0", {"start": v(-1774.83, 130.18) * mm, "end": v(-1774.82, 301.63) * mm});
            skLineSegment(sketch, "E119.1", {"start": v(-1774.83, 130.18) * mm, "end": v(-1603.37, 130.18) * mm});
            skLineSegment(sketch, "E119.2", {"start": v(-1603.37, 301.63) * mm, "end": v(-1603.37, 130.18) * mm});
            skLineSegment(sketch, "E119.3", {"start": v(-1603.37, 301.63) * mm, "end": v(-1774.82, 301.63) * mm});
            skLineSegment(sketch, "E120.0", {"start": v(-1774.82, 320.68) * mm, "end": v(-1774.82, 492.13) * mm});
            skLineSegment(sketch, "E120.1", {"start": v(-1603.37, 320.68) * mm, "end": v(-1774.82, 320.68) * mm});
            skLineSegment(sketch, "E120.2", {"start": v(-1603.37, 492.13) * mm, "end": v(-1603.37, 320.68) * mm});
            skLineSegment(sketch, "E120.3", {"start": v(-1774.82, 492.13) * mm, "end": v(-1603.37, 492.13) * mm});
            skLineSegment(sketch, "E121.0", {"start": v(-1774.82, 682.63) * mm, "end": v(-1603.37, 682.63) * mm});
            skLineSegment(sketch, "E121.1", {"start": v(-1774.82, 511.18) * mm, "end": v(-1774.82, 682.63) * mm});
            skLineSegment(sketch, "E121.2", {"start": v(-1774.82, 511.18) * mm, "end": v(-1603.37, 511.18) * mm});
            skLineSegment(sketch, "E121.3", {"start": v(-1603.37, 682.63) * mm, "end": v(-1603.37, 511.18) * mm});
            skSolve(sketch);
        }
        {
            var Q0;
            Q0=makeQuery(id+"F36.imprint","IMPRINT",FACE,{"disambiguationData":[TD([[makeQuery(id+"F36.imprint","IMPRINT",EDGE,{"derivedFrom":sQuery(id+"F36.wireOp",EDGE,"E111.0")}),-1.0]])]});
            var Q1;
            Q1=makeQuery(id+"F36.imprint","IMPRINT",FACE,{"disambiguationData":[TD([[makeQuery(id+"F36.imprint","IMPRINT",EDGE,{"derivedFrom":sQuery(id+"F36.wireOp",EDGE,"E91.0")}),-1.0]])]});
            var Q2;
            Q2=makeQuery(id+"F36.imprint","IMPRINT",FACE,{"disambiguationData":[TD([[makeQuery(id+"F36.imprint","IMPRINT",EDGE,{"derivedFrom":sQuery(id+"F36.wireOp",EDGE,"E95.0.2")}),1.0]])]});
            var Q3;
            Q3=makeQuery(id+"F36.imprint","IMPRINT",FACE,{"disambiguationData":[TD([[makeQuery(id+"F36.imprint","IMPRINT",EDGE,{"derivedFrom":sQuery(id+"F36.wireOp",EDGE,"E103.0")}),1.0]])]});
            var Q4;
            Q4=makeQuery(id+"F36.imprint","IMPRINT",FACE,{"disambiguationData":[TD([[makeQuery(id+"F36.imprint","IMPRINT",EDGE,{"derivedFrom":sQuery(id+"F36.wireOp",EDGE,"E104.0")}),1.0]])]});
            var Q5;
            Q5=makeQuery(id+"F36.imprint","IMPRINT",FACE,{"disambiguationData":[TD([[makeQuery(id+"F36.imprint","IMPRINT",EDGE,{"derivedFrom":sQuery(id+"F36.wireOp",EDGE,"E98.0.2")}),-1.0]])]});
            extrude(context, id + "F37", {"entities" : qUnion([Q0, Q1, Q2, Q3, Q4, Q5]), "operationType" : NewBodyOperationType.REMOVE, "oppositeDirection" : true, "depth" : 31.75 * mm, "offsetDistance" : 25.4 * mm});
        }
        {
            var Q0;
            Q0=qCreatedBy(makeId("Top.planeOp"),FACE);
            var sketch = newSketch(context, id + "F38", { "sketchPlane" : qUnion([Q0])});
            skLineSegment(sketch, "E122.bottom", {"start": v(431.96, -135.03) * mm, "end": v(603.4, -135.03) * mm});
            skLineSegment(sketch, "E122.top", {"start": v(431.96, 36.42) * mm, "end": v(603.4, 36.42) * mm});
            skLineSegment(sketch, "E122.left", {"start": v(431.96, -135.03) * mm, "end": v(431.96, 36.42) * mm});
            skLineSegment(sketch, "E122.right", {"start": v(603.4, -135.03) * mm, "end": v(603.4, 36.42) * mm});
            skSolve(sketch);
        }
        {
            var Q0;
            Q0 = qSketchRegion(id + "F38", true);
            extrude(context, id + "F39", {"entities" : qUnion([Q0]), "depth" : 6.35 * mm, "offsetDistance" : 25.4 * mm});
        }
        {
            var Q0;
            Q0=qCreatedBy(makeId("Front.planeOp"),FACE);
            var sketch = newSketch(context, id + "F40", { "sketchPlane" : qUnion([Q0])});
            skCircle(sketch, "E123", {"center": v(343.28, 316.3) * mm, "radius": 12.7 * mm});
            skSolve(sketch);
        }
        {
            var Q0;
            Q0 = qSketchRegion(id + "F40", true);
            extrude(context, id + "F41", {"entities" : qUnion([Q0]), "depth" : 38.1 * mm, "offsetDistance" : 25.4 * mm});
        }
        {
            var Q0;
            Q0=makeQuery(id+"F41.opExtrude","CAP_FACE",FACE,{"disambiguationData":[OSD([sQuery(id+"F40.wireOp",EDGE,"E123")])],"isStart":false});
            var sketch = newSketch(context, id + "F42", { "sketchPlane" : qUnion([Q0])});
            skLineSegment(sketch, "E124.bottom", {"start": v(349.63, 340.9) * mm, "end": v(336.93, 340.9) * mm});
            skLineSegment(sketch, "E124.top", {"start": v(349.63, 291.73) * mm, "end": v(336.93, 291.73) * mm});
            skLineSegment(sketch, "E124.left", {"start": v(349.63, 340.9) * mm, "end": v(349.63, 291.73) * mm});
            skLineSegment(sketch, "E124.right", {"start": v(336.93, 340.9) * mm, "end": v(336.93, 291.73) * mm});
            skPoint(sketch, "E124.middle", {"position": v(343.28, 316.3) * mm});
            skSolve(sketch);
        }
        {
            var Q0;
            Q0 = qSketchRegion(id + "F42", true);
            extrude(context, id + "F43", {"entities" : qUnion([Q0]), "operationType" : NewBodyOperationType.REMOVE, "oppositeDirection" : true, "depth" : 12.7 * mm, "offsetDistance" : 25.4 * mm});
        }
        {
            var Q0;
            Q0=makeQuery(id+"F43.boolean.opBoolean","COPY",FACE,{"derivedFrom":makeQuery(id+"F43.opExtrude","SWEPT_FACE",FACE,{"disambiguationData":[OSD([sQuery(id+"F42.wireOp",EDGE,"E124.right")])]})});
            var sketch = newSketch(context, id + "F44", { "sketchPlane" : qUnion([Q0])});
            skLineSegment(sketch, "E125", {"start": v(-31.75, 327.3) * mm, "end": v(-31.75, 305.31) * mm});
            skCircle(sketch, "E126", {"center": v(-31.75, 316.3) * mm, "radius": 3.81 * mm});
            skSolve(sketch);
        }
        {
            var Q0;
            Q0 = qSketchRegion(id + "F44", true);
            extrude(context, id + "F45", {"entities" : qUnion([Q0]), "operationType" : NewBodyOperationType.REMOVE, "endBound" : BoundingType.SYMMETRIC, "depth" : 79.25 * mm, "offsetDistance" : 25.4 * mm});
        }
        {
            var Q0;
            Q0=qCreatedBy(makeId("Front.planeOp"),FACE);
            var sketch = newSketch(context, id + "F46", { "sketchPlane" : qUnion([Q0])});
            skLineSegment(sketch, "E127.bottom", {"start": v(443.38, 338.25) * mm, "end": v(430.68, 338.25) * mm});
            skLineSegment(sketch, "E127.top", {"start": v(443.38, 363.65) * mm, "end": v(430.68, 363.65) * mm});
            skLineSegment(sketch, "E127.left", {"start": v(443.38, 338.25) * mm, "end": v(443.38, 363.65) * mm});
            skLineSegment(sketch, "E127.right", {"start": v(430.68, 338.25) * mm, "end": v(430.68, 363.65) * mm});
            skPoint(sketch, "E127.middle", {"position": v(437.03, 350.95) * mm});
            skSolve(sketch);
        }
        {
            var Q0;
            Q0 = qSketchRegion(id + "F46", true);
            extrude(context, id + "F47", {"entities" : qUnion([Q0]), "depth" : 50.8 * mm, "offsetDistance" : 25.4 * mm});
        }
        {
            var Q0;
            Q0=makeQuery(id+"F47.opExtrude","SWEPT_FACE",FACE,{"disambiguationData":[OSD([sQuery(id+"F46.wireOp",EDGE,"E127.left")])]});
            cPlane(context, id + "F48", {"entities" : qUnion([Q0]), "cplaneType" : CPlaneType.OFFSET, "offset" : 6.35 * mm, "oppositeDirection" : true, "width" : 152.4 * mm, "height" : 152.4 * mm});
        }
        {
            var Q0;
            Q0=qCreatedBy(id+"F48.planeOp",FACE);
            var sketch = newSketch(context, id + "F49", { "sketchPlane" : qUnion([Q0])});
            skLineSegment(sketch, "E128", {"start": v(0, 363.65) * mm, "end": v(0, 338.25) * mm});
            skCircle(sketch, "E129", {"center": v(-6.35, 350.95) * mm, "radius": 3.81 * mm});
            skPoint(sketch, "E129.centerSnap0", {"position": v(0, 350.95) * mm});
            skSolve(sketch);
        }
        {
            var Q0;
            Q0 = qSketchRegion(id + "F49", true);
            extrude(context, id + "F50", {"entities" : qUnion([Q0]), "operationType" : NewBodyOperationType.ADD, "endBound" : BoundingType.SYMMETRIC, "depth" : 25.4 * mm, "offsetDistance" : 25.4 * mm});
        }
        {
            var Q0;
            Q0=makeQuery(id+"F47.opExtrude","CAP_EDGE",EDGE,{"disambiguationData":[OSD([sQuery(id+"F46.wireOp",EDGE,"E127.top")])],"isStart":true});
            var Q1;
            Q1=makeQuery(id+"F47.opExtrude","CAP_EDGE",EDGE,{"disambiguationData":[OSD([sQuery(id+"F46.wireOp",EDGE,"E127.bottom")])],"isStart":true});
            fillet(context, id + "F51", {"entities" : qUnion([Q0, Q1]), "radius" : 12.7 * mm, "tangentPropagation" : true, "allowEdgeOverflow" : false});
        }
        {
            var Q0;
            Q0=makeQuery(id+"F47.opExtrude","SWEPT_FACE",FACE,{"disambiguationData":[OSD([sQuery(id+"F46.wireOp",EDGE,"E127.left")])]});
            var sketch = newSketch(context, id + "F52", { "sketchPlane" : qUnion([Q0])});
            skLineSegment(sketch, "E130", {"start": v(-50.8, 363.65) * mm, "end": v(-40.98, 363.65) * mm});
            skLineSegment(sketch, "E131", {"start": v(-40.98, 363.65) * mm, "end": v(-40.98, 338.25) * mm});
            skLineSegment(sketch, "E132", {"start": v(-40.98, 338.25) * mm, "end": v(-50.8, 338.25) * mm});
            skLineSegment(sketch, "E133", {"start": v(-50.8, 338.25) * mm, "end": v(-50.8, 363.65) * mm});
            skSolve(sketch);
        }
        {
            var Q0;
            Q0 = qSketchRegion(id + "F52", true);
            extrude(context, id + "F53", {"entities" : qUnion([Q0]), "operationType" : NewBodyOperationType.ADD, "depth" : 6.35 * mm, "offsetDistance" : 25.4 * mm});
        }
        {
            var Q0;
            Q0=makeQuery(id+"F53.opExtrude","CAP_FACE",FACE,{"disambiguationData":[OSD([sQuery(id+"F52.wireOp",EDGE,"E130"),sQuery(id+"F52.wireOp",EDGE,"E131"),sQuery(id+"F52.wireOp",EDGE,"E132"),sQuery(id+"F52.wireOp",EDGE,"E133")])],"isStart":false});
            var sketch = newSketch(context, id + "F54", { "sketchPlane" : qUnion([Q0])});
            skLineSegment(sketch, "E134", {"start": v(-45.89, 363.65) * mm, "end": v(-45.89, 338.25) * mm});
            skCircle(sketch, "E135", {"center": v(-45.89, 350.95) * mm, "radius": 3.81 * mm});
            skSolve(sketch);
        }
        {
            var Q0;
            Q0 = qSketchRegion(id + "F54", true);
            extrude(context, id + "F55", {"entities" : qUnion([Q0]), "operationType" : NewBodyOperationType.ADD, "depth" : 12.7 * mm, "offsetDistance" : 25.4 * mm});
        }
        {
            var Q0;
            Q0=makeQuery(id+"F28.opRevolve","SWEPT_FACE",FACE,{"disambiguationData":[OSD([sQuery(id+"F27.wireOp",EDGE,"E76")])]});
            var sketch = newSketch(context, id + "F56", { "sketchPlane" : qUnion([Q0])});
            skCircle(sketch, "E136", {"center": v(0, 1520.1) * mm, "radius": 26.99 * mm});
            skSolve(sketch);
        }
        {
            var Q0;
            Q0 = qSketchRegion(id + "F56", true);
            extrude(context, id + "F57", {"entities" : qUnion([Q0]), "operationType" : NewBodyOperationType.ADD, "depth" : 19.05 * mm, "offsetDistance" : 25.4 * mm});
        }
        {
            var Q0;
            Q0=makeQuery(id+"F57.opExtrude","CAP_FACE",FACE,{"disambiguationData":[OSD([sQuery(id+"F56.wireOp",EDGE,"E136")])],"isStart":false});
            var sketch = newSketch(context, id + "F58", { "sketchPlane" : qUnion([Q0])});
            skCircle(sketch, "E137", {"center": v(0, 1520.1) * mm, "radius": 19.77 * mm});
            skPoint(sketch, "E138", {"position": v(0, 1500.32) * mm});
            skCircle(sketch, "E139", {"center": v(0, 1500.32) * mm, "radius": 3.81 * mm});
            skSolve(sketch);
        }
        {
            var Q0;
            {var subQ0=sQuery(id+"F58.wireOp",EDGE,"E139");var subQ1=sQuery(id+"F58.wireOp",EDGE,"E137");var subQ2=makeQuery(id+"F58.imprint","INTERSECT",VERTEX,{"disambiguationData":[OD(0.0)],"derivedFrom":[subQ1,subQ0]});Q0=makeQuery(id+"F58.imprint","IMPRINT",FACE,{"disambiguationData":[TD([[makeQuery(id+"F58.imprint","IMPRINT",EDGE,{"disambiguationData":[TD([[subQ2,-1.0]])],"derivedFrom":subQ1}),1.0]])]});}
            var Q1;
            {var subQ0=sQuery(id+"F58.wireOp",EDGE,"E139");var subQ1=sQuery(id+"F58.wireOp",EDGE,"E137");var subQ2=makeQuery(id+"F58.imprint","INTERSECT",VERTEX,{"disambiguationData":[OD(0.0)],"derivedFrom":[subQ1,subQ0]});Q1=makeQuery(id+"F58.imprint","IMPRINT",FACE,{"disambiguationData":[TD([[makeQuery(id+"F58.imprint","IMPRINT",EDGE,{"disambiguationData":[TD([[subQ2,-1.0]])],"derivedFrom":subQ1}),-1.0]])]});}
            extrude(context, id + "F59", {"entities" : qUnion([Q0, Q1]), "operationType" : NewBodyOperationType.REMOVE, "oppositeDirection" : true, "depth" : 12.7 * mm, "offsetDistance" : 25.4 * mm});
        }
    });
